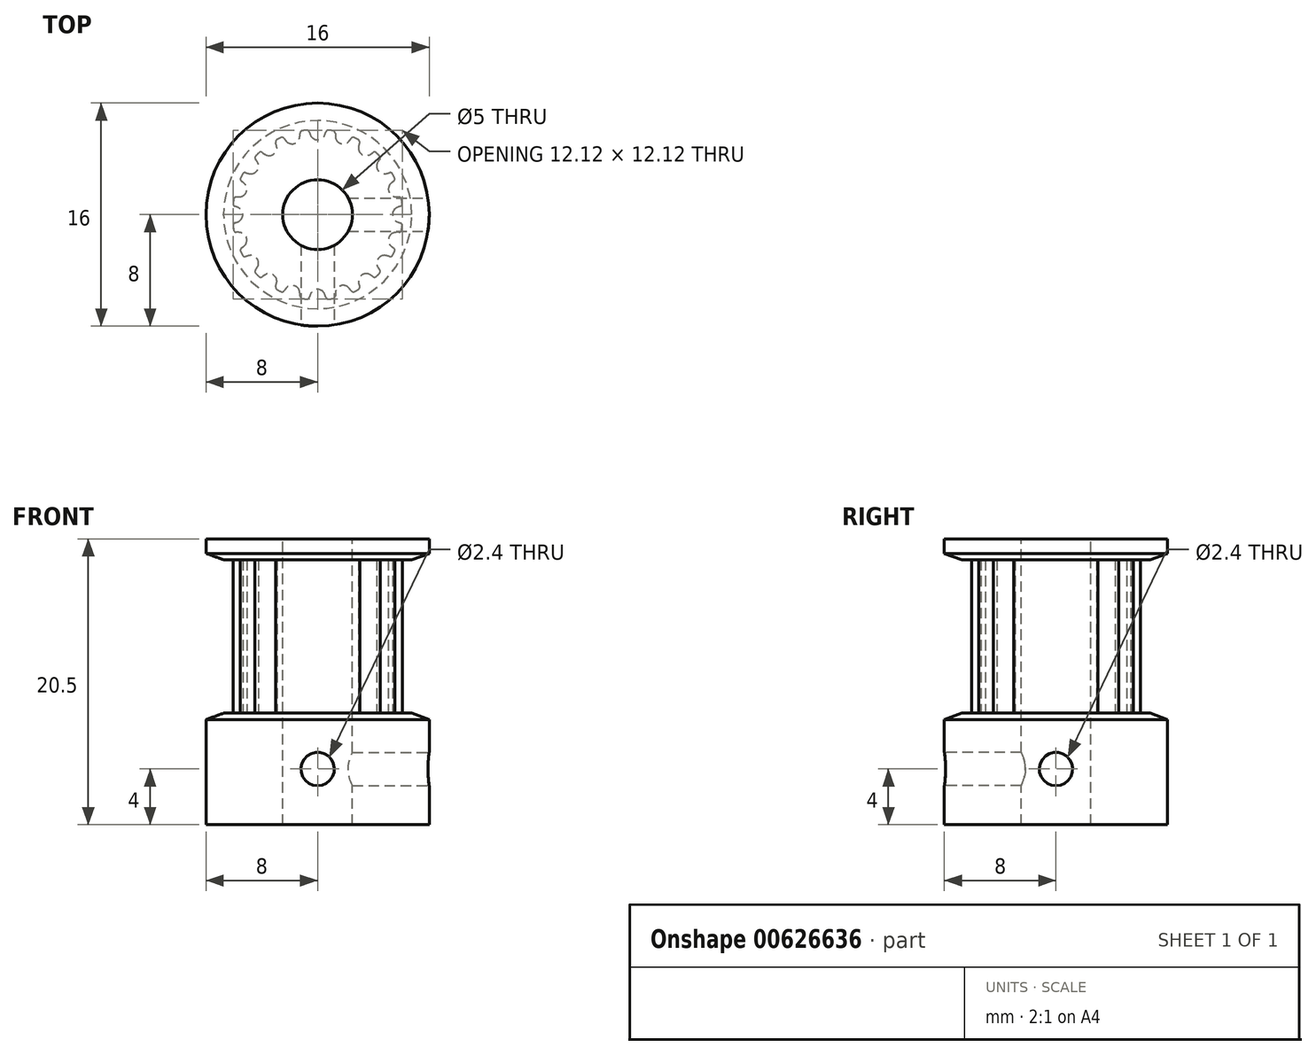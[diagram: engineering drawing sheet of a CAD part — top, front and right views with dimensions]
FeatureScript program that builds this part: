
annotation { "Feature Type Name" : "Feature", "Feature Type Description" : "" }
export const myFeature = defineFeature(function(context is Context, id is Id, definition is map)
    precondition{}
    {
        {
            assignVariable(context, id + "F0", {"name" : "teeth", "anyValue" : 20});
        }
        {
            assignVariable(context, id + "F1", {"name" : "bore_diameter", "anyValue" : 5 * mm});
        }
        {
            var Q0;
            Q0=qCreatedBy(makeId("Top.planeOp"),FACE);
            var sketch = newSketch(context, id + "F2", { "sketchPlane" : qUnion([Q0])});
            skLineSegment(sketch, "E0", {"start": v(0, 0) * mm, "end": v(0, 5.36) * mm, "construction": true});
            skCircle(sketch, "E1", {"center": v(0, 0) * mm, "radius": 6.11 * mm});
            skPoint(sketch, "E2.MirrorCS.end.orphan", {"position": v(0.96, 6.04) * mm});
            skLineSegment(sketch, "E3", {"start": v(0.96, 6.04) * mm, "end": v(1, 6.29) * mm, "construction": true});
            skLineSegment(sketch, "E4", {"start": v(-0.96, 6.04) * mm, "end": v(-1, 6.29) * mm, "construction": true});
            skArc(sketch, "E5", {"start": v(0, 5.36) * mm, "mid": v(0.31, 5.46) * mm, "end": v(0.52, 5.72) * mm});
            skArc(sketch, "E6", {"start": v(0.52, 5.72) * mm, "mid": v(0.56, 5.83) * mm, "end": v(0.58, 5.94) * mm, "construction": true});
            skLineSegment(sketch, "E7", {"start": v(0, 5.36) * mm, "end": v(0, 6.11) * mm, "construction": true});
            skLineSegment(sketch, "E8", {"start": v(0, 6.11) * mm, "end": v(0, 6.37) * mm, "construction": true});
            skArc(sketch, "E9", {"start": v(0.58, 5.94) * mm, "mid": v(0.64, 6.04) * mm, "end": v(0.75, 6.07) * mm, "construction": true});
            skArc(sketch, "E10", {"start": v(1, 6.29) * mm, "mid": v(0, 6.37) * mm, "end": v(-1, 6.29) * mm, "construction": true});
            skLineSegment(sketch, "E11", {"start": v(0.96, 6.04) * mm, "end": v(0.84, 5.3) * mm});
            skLineSegment(sketch, "E12", {"start": v(0.84, 5.3) * mm, "end": v(0, 0) * mm});
            skLineSegment(sketch, "E13", {"start": v(0, 0) * mm, "end": v(-0.84, 5.3) * mm});
            skLineSegment(sketch, "E14", {"start": v(-0.84, 5.3) * mm, "end": v(-0.96, 6.04) * mm});
            skArc(sketch, "E15", {"start": v(0.8, 6.06) * mm, "mid": v(0.67, 6.03) * mm, "end": v(0.6, 5.93) * mm});
            skArc(sketch, "E16", {"start": v(0.52, 5.72) * mm, "mid": v(0.56, 5.83) * mm, "end": v(0.6, 5.93) * mm});
            skArc(sketch, "E17.MirrorCS", {"start": v(0, 5.36) * mm, "mid": v(-0.31, 5.46) * mm, "end": v(-0.52, 5.72) * mm});
            skArc(sketch, "E18.MirrorCS", {"start": v(-0.52, 5.72) * mm, "mid": v(-0.56, 5.83) * mm, "end": v(-0.6, 5.93) * mm});
            skArc(sketch, "E19.MirrorCS", {"start": v(-0.8, 6.06) * mm, "mid": v(-0.67, 6.03) * mm, "end": v(-0.6, 5.93) * mm});
            skArc(sketch, "E20", {"start": v(0, 6.11) * mm, "mid": v(-0.2, 6.1) * mm, "end": v(-0.4, 6.1) * mm});
            skArc(sketch, "E21", {"start": v(0.84, 5.3) * mm, "mid": v(0, 5.36) * mm, "end": v(-0.84, 5.3) * mm, "construction": true});
            skLineSegment(sketch, "E22", {"start": v(1, 6.29) * mm, "end": v(1.05, 6.66) * mm, "construction": true});
            skLineSegment(sketch, "E23", {"start": v(-1, 6.29) * mm, "end": v(-1.05, 6.66) * mm, "construction": true});
            skArc(sketch, "E24", {"start": v(-1.05, 6.66) * mm, "mid": v(0, 6.74) * mm, "end": v(1.05, 6.66) * mm, "construction": true});
            skSolve(sketch);
        }
        {
            var Q0;
            Q0=makeQuery(id+"F2.imprint","IMPRINT",FACE,{"disambiguationData":[TD([[makeQuery(id+"F2.imprint","IMPRINT",EDGE,{"derivedFrom":sQuery(id+"F2.wireOp",EDGE,"E5")}),-1.0]])]});
            var Q1;
            {var subQ1=sQuery(id+"F2.wireOp",EDGE,"E14");Q1=makeQuery(id+"F2.imprint","IMPRINT",FACE,{"disambiguationData":[TD([[makeQuery(id+"F2.imprint","IMPRINT",EDGE,{"derivedFrom":subQ1}),-1.0]])]});}
            var Q2;
            {var subQ0=sQuery(id+"F2.wireOp",EDGE,"E12");Q2=makeQuery(id+"F2.imprint","IMPRINT",FACE,{"disambiguationData":[TD([[makeQuery(id+"F2.imprint","IMPRINT",EDGE,{"derivedFrom":subQ0}),-1.0]])]});}
            extrude(context, id + "F3", {"entities" : qUnion([Q0, Q1, Q2]), "depth" : 11 * mm, "symmetric" : true});
        }
        {
            var Q0;
            Q0=makeQuery(id+"F3.opExtrude","SWEPT_BODY",BODY,{"disambiguationData":[OSD([sQuery(id+"F2.wireOp",EDGE,"E1"),sQuery(id+"F2.wireOp",EDGE,"E5"),sQuery(id+"F2.wireOp",EDGE,"E11"),sQuery(id+"F2.wireOp",EDGE,"E12"),sQuery(id+"F2.wireOp",EDGE,"E13"),sQuery(id+"F2.wireOp",EDGE,"E14"),sQuery(id+"F2.wireOp",EDGE,"E15"),sQuery(id+"F2.wireOp",EDGE,"E16"),sQuery(id+"F2.wireOp",EDGE,"E17.MirrorCS"),sQuery(id+"F2.wireOp",EDGE,"E18.MirrorCS"),sQuery(id+"F2.wireOp",EDGE,"E19.MirrorCS")])]});
            var Q1;
            Q1=makeQuery(id+"F3.opExtrude","SWEPT_EDGE",EDGE,{"disambiguationData":[OSD([sQuery(id+"F2.wireOp",EDGE,"E12"),sQuery(id+"F2.wireOp",EDGE,"E13")])]});
            circularPattern(context, id + "F4", {"operationType" : NewBodyOperationType.ADD, "entities" : qUnion([Q0]), "axis" : qUnion([Q1]), "angle" : 360 * degree, "instanceCount" : getVariable(context, 'teeth'), "equalSpace" : true});
        }
        {
            var Q0;
            Q0=qCreatedBy(makeId("Front.planeOp"),FACE);
            var sketch = newSketch(context, id + "F5", { "sketchPlane" : qUnion([Q0])});
            skLineSegment(sketch, "E25", {"start": v(0, -5.5) * mm, "end": v(6.74, -5.5) * mm});
            skLineSegment(sketch, "E26", {"start": v(6.74, -5.5) * mm, "end": v(8, -5.96) * mm});
            skLineSegment(sketch, "E27", {"start": v(8, -5.96) * mm, "end": v(8, -13.5) * mm});
            skLineSegment(sketch, "E28", {"start": v(8, -13.5) * mm, "end": v(0, -13.5) * mm});
            skLineSegment(sketch, "E29", {"start": v(0, -13.5) * mm, "end": v(0, -5.5) * mm});
            skLineSegment(sketch, "E30", {"start": v(0, 5.5) * mm, "end": v(6.74, 5.5) * mm});
            skLineSegment(sketch, "E31", {"start": v(8, 5.96) * mm, "end": v(6.74, 5.5) * mm});
            skLineSegment(sketch, "E32", {"start": v(8, 5.96) * mm, "end": v(8, 7) * mm});
            skLineSegment(sketch, "E33", {"start": v(8, 7) * mm, "end": v(0, 7) * mm});
            skLineSegment(sketch, "E34", {"start": v(0, 7) * mm, "end": v(0, 5.5) * mm});
            skLineSegment(sketch, "E35", {"start": v(6.74, -5.5) * mm, "end": v(8, -5.5) * mm, "construction": true});
            skLineSegment(sketch, "E36", {"start": v(8, -5.5) * mm, "end": v(8, -5.96) * mm, "construction": true});
            skLineSegment(sketch, "E37", {"start": v(6.74, 5.5) * mm, "end": v(8, 5.5) * mm, "construction": true});
            skLineSegment(sketch, "E38", {"start": v(8, 5.5) * mm, "end": v(8, 5.96) * mm, "construction": true});
            skLineSegment(sketch, "E39", {"start": v(6.11, 0) * mm, "end": v(6.11, -5.5) * mm, "construction": true});
            skSolve(sketch);
        }
        {
            var Q0;
            Q0=qSketchRegion(id+"F5",true);
            var Q1;
            Q1=qConstructionFilter(qBodyType(qCreatedBy(id+"F5",EDGE),BodyType.WIRE),ConstructionObject.NO);
            var Q2;
            Q2=sQuery(id+"F5.wireOp",EDGE,"E29");
            revolve(context, id + "F6", {"operationType" : NewBodyOperationType.ADD, "entities" : qUnion([Q0]), "surfaceEntities" : qUnion([Q1]), "axis" : qUnion([Q2]), "revolveType" : RevolveType.FULL});
        }
        {
            var Q0;
            Q0=makeQuery(id+"F6.opRevolve","SWEPT_FACE",FACE,{"disambiguationData":[OSD([sQuery(id+"F5.wireOp",EDGE,"E28")])]});
            var sketch = newSketch(context, id + "F7", { "sketchPlane" : qUnion([Q0])});
            skPoint(sketch, "E40", {"position": v(0, 0) * mm});
            skSolve(sketch);
        }
        {
            var Q0;
            Q0=sQuery(id+"F7.wireOp",VERTEX,"E40");
            var Q1;
            Q1=makeQuery(id+"F3.opExtrude","SWEPT_BODY",BODY,{"disambiguationData":[OSD([sQuery(id+"F2.wireOp",EDGE,"E1"),sQuery(id+"F2.wireOp",EDGE,"E5"),sQuery(id+"F2.wireOp",EDGE,"E11"),sQuery(id+"F2.wireOp",EDGE,"E12"),sQuery(id+"F2.wireOp",EDGE,"E13"),sQuery(id+"F2.wireOp",EDGE,"E14"),sQuery(id+"F2.wireOp",EDGE,"E15"),sQuery(id+"F2.wireOp",EDGE,"E16"),sQuery(id+"F2.wireOp",EDGE,"E17.MirrorCS"),sQuery(id+"F2.wireOp",EDGE,"E18.MirrorCS"),sQuery(id+"F2.wireOp",EDGE,"E19.MirrorCS")])]});
            hole(context, id + "F8", {"style" : HoleStyle.SIMPLE, "holeDiameter" : getVariable(context, 'bore_diameter'), "endStyle" : HoleEndStyle.THROUGH, "locations" : qUnion([Q0]), "scope" : qUnion([Q1]), "isTappedThrough" : true});
        }
        {
            var Q0;
            Q0=qCreatedBy(makeId("Front.planeOp"),FACE);
            var sketch = newSketch(context, id + "F9", { "sketchPlane" : qUnion([Q0])});
            skPoint(sketch, "E41", {"position": v(0, -9.5) * mm});
            skLineSegment(sketch, "E42", {"start": v(0, -13.5) * mm, "end": v(0, -5.5) * mm});
            skSolve(sketch);
        }
        {
            var Q0;
            Q0=qCreatedBy(makeId("Right.planeOp"),FACE);
            var sketch = newSketch(context, id + "F10", { "sketchPlane" : qUnion([Q0])});
            skPoint(sketch, "E43", {"position": v(0, -9.5) * mm});
            skSolve(sketch);
        }
        {
            var Q0;
            Q0=sQuery(id+"F9.wireOp",VERTEX,"E41");
            var Q1;
            Q1=makeQuery(id+"F3.opExtrude","SWEPT_BODY",BODY,{"disambiguationData":[OSD([sQuery(id+"F2.wireOp",EDGE,"E1"),sQuery(id+"F2.wireOp",EDGE,"E5"),sQuery(id+"F2.wireOp",EDGE,"E11"),sQuery(id+"F2.wireOp",EDGE,"E12"),sQuery(id+"F2.wireOp",EDGE,"E13"),sQuery(id+"F2.wireOp",EDGE,"E14"),sQuery(id+"F2.wireOp",EDGE,"E15"),sQuery(id+"F2.wireOp",EDGE,"E16"),sQuery(id+"F2.wireOp",EDGE,"E17.MirrorCS"),sQuery(id+"F2.wireOp",EDGE,"E18.MirrorCS"),sQuery(id+"F2.wireOp",EDGE,"E19.MirrorCS")])]});
            hole(context, id + "F11", {"style" : HoleStyle.SIMPLE, "endStyle" : HoleEndStyle.THROUGH, "oppositeDirection" : true, "standardTappedOrClearance" : lookupTablePath({ "standard" : "ISO", "engagement" : "75%", "pitch" : "0.6 mm", "size" : "M3", "type" : "Tapped" }), "standardBlindInLast" : lookupTablePath({ "standard" : "ISO", "engagement" : "75%", "pitch" : "0.6 mm", "size" : "M3", "type" : "Tapped" }), "holeDiameter" : 2.4 * mm, "locations" : qUnion([Q0]), "scope" : qUnion([Q1]), "isTappedThrough" : true, "showTappedDepth" : true});
        }
        {
            var Q0;
            Q0=sQuery(id+"F10.wireOp",VERTEX,"E43");
            var Q1;
            Q1=makeQuery(id+"F3.opExtrude","SWEPT_BODY",BODY,{"disambiguationData":[OSD([sQuery(id+"F2.wireOp",EDGE,"E1"),sQuery(id+"F2.wireOp",EDGE,"E5"),sQuery(id+"F2.wireOp",EDGE,"E11"),sQuery(id+"F2.wireOp",EDGE,"E12"),sQuery(id+"F2.wireOp",EDGE,"E13"),sQuery(id+"F2.wireOp",EDGE,"E14"),sQuery(id+"F2.wireOp",EDGE,"E15"),sQuery(id+"F2.wireOp",EDGE,"E16"),sQuery(id+"F2.wireOp",EDGE,"E17.MirrorCS"),sQuery(id+"F2.wireOp",EDGE,"E18.MirrorCS"),sQuery(id+"F2.wireOp",EDGE,"E19.MirrorCS")])]});
            hole(context, id + "F12", {"style" : HoleStyle.SIMPLE, "endStyle" : HoleEndStyle.THROUGH, "oppositeDirection" : true, "standardTappedOrClearance" : lookupTablePath({ "standard" : "ISO", "engagement" : "75%", "pitch" : "0.6 mm", "size" : "M3", "type" : "Tapped" }), "standardBlindInLast" : lookupTablePath({ "standard" : "ISO", "engagement" : "75%", "pitch" : "0.6 mm", "size" : "M3", "type" : "Tapped" }), "holeDiameter" : 2.4 * mm, "locations" : qUnion([Q0]), "scope" : qUnion([Q1]), "isTappedThrough" : true, "showTappedDepth" : true});
        }
    });
